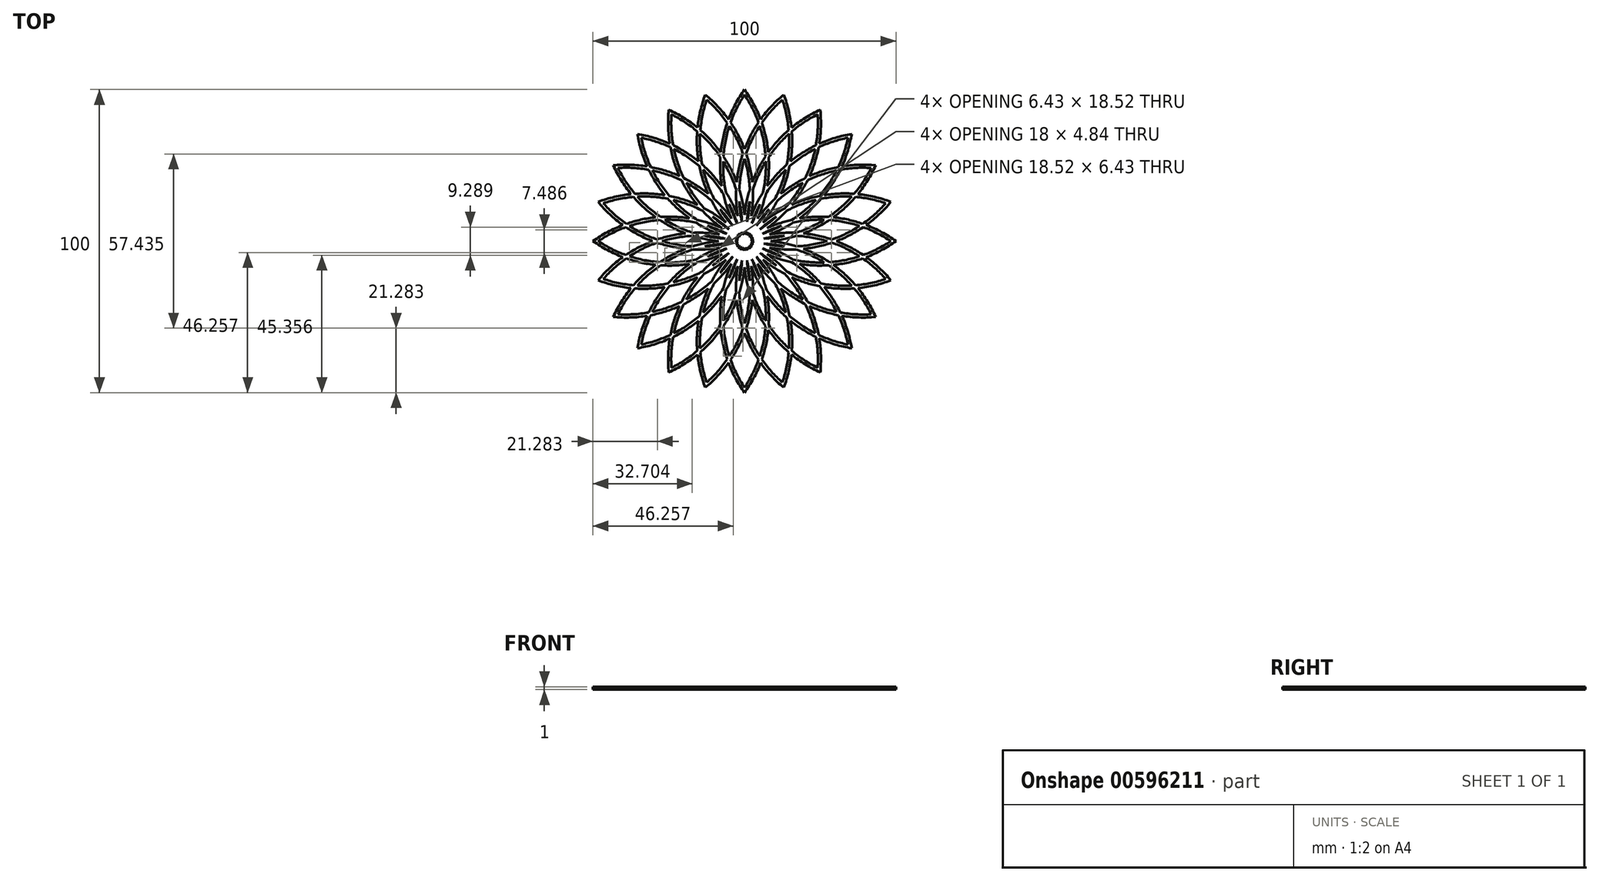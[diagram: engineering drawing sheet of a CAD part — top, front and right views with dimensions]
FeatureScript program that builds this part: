
annotation { "Feature Type Name" : "Feature", "Feature Type Description" : "" }
export const myFeature = defineFeature(function(context is Context, id is Id, definition is map)
    precondition{}
    {
        {
            var Q0;
            Q0=qCreatedBy(makeId("Top.planeOp"),FACE);
            var sketch = newSketch(context, id + "F0", { "sketchPlane" : qUnion([Q0])});
            skArc(sketch, "E0.1", {"start": v(0.29, 2.19) * mm, "mid": v(0.55, 2.6) * mm, "end": v(0.8, 3) * mm});
            skArc(sketch, "E1.22.1", {"start": v(24.12, 41.78) * mm, "mid": v(19.7, 39.26) * mm, "end": v(15.6, 36.21) * mm});
            skArc(sketch, "E1.22.3", {"start": v(25, 43.3) * mm, "mid": v(20.06, 40.68) * mm, "end": v(15.5, 37.43) * mm});
            skArc(sketch, "E1.23.1", {"start": v(12.49, 46.6) * mm, "mid": v(8.86, 43.02) * mm, "end": v(5.7, 39.02) * mm});
            skArc(sketch, "E1.23.3", {"start": v(12.94, 48.3) * mm, "mid": v(8.85, 44.48) * mm, "end": v(5.29, 40.16) * mm});
            skPoint(sketch, "E1.center", {"position": v(0, 0) * mm});
            skLineSegment(sketch, "E2", {"start": v(25, 43.3) * mm, "end": v(0, 0) * mm, "construction": true});
            skArc(sketch, "E3.trimOffspring", {"start": v(4.6, 39.17) * mm, "mid": v(2.04, 34.88) * mm, "end": v(0, 30.33) * mm});
            skArc(sketch, "E4.trimOffspring", {"start": v(5.29, 40.16) * mm, "mid": v(2.97, 45.26) * mm, "end": v(0, 50) * mm});
            skArc(sketch, "E5.trimOffspring", {"start": v(4.6, 39.17) * mm, "mid": v(2.57, 43.85) * mm, "end": v(0, 48.25) * mm});
            skArc(sketch, "E6.trimOffspring", {"start": v(5, 37.98) * mm, "mid": v(2.49, 33.55) * mm, "end": v(0.53, 28.85) * mm});
            skArc(sketch, "E7.trimOffspring", {"start": v(14.57, 36.64) * mm, "mid": v(11, 33.17) * mm, "end": v(7.85, 29.3) * mm});
            skArc(sketch, "E8.trimOffspring", {"start": v(15.5, 37.43) * mm, "mid": v(14.58, 42.95) * mm, "end": v(12.94, 48.3) * mm});
            skArc(sketch, "E9.trimOffspring", {"start": v(14.66, 35.39) * mm, "mid": v(11.08, 31.76) * mm, "end": v(7.98, 27.73) * mm});
            skArc(sketch, "E10.trimOffspring", {"start": v(14.57, 36.64) * mm, "mid": v(13.83, 41.69) * mm, "end": v(12.49, 46.6) * mm});
            skArc(sketch, "E11.trimOffspring", {"start": v(7.85, 29.3) * mm, "mid": v(7.06, 34.22) * mm, "end": v(5.7, 39.02) * mm});
            skArc(sketch, "E12.trimOffspring", {"start": v(6.96, 28) * mm, "mid": v(4.52, 23.86) * mm, "end": v(2.56, 19.46) * mm});
            skArc(sketch, "E13.trimOffspring", {"start": v(6.96, 28) * mm, "mid": v(6.28, 33.05) * mm, "end": v(5, 37.98) * mm});
            skArc(sketch, "E14.trimOffspring", {"start": v(7.05, 26.3) * mm, "mid": v(4.6, 21.75) * mm, "end": v(2.74, 16.93) * mm});
            skArc(sketch, "E15.trimOffspring", {"start": v(13.97, 25.25) * mm, "mid": v(10.54, 21.87) * mm, "end": v(7.51, 18.13) * mm});
            skArc(sketch, "E16.trimOffspring", {"start": v(13.97, 25.25) * mm, "mid": v(14.62, 30.3) * mm, "end": v(14.66, 35.39) * mm});
            skArc(sketch, "E17.trimOffspring", {"start": v(2.56, 19.46) * mm, "mid": v(1.8, 24.21) * mm, "end": v(0.53, 28.85) * mm});
            skArc(sketch, "E18.trimOffspring", {"start": v(1.73, 17.07) * mm, "mid": v(0.65, 12.87) * mm, "end": v(0, 8.59) * mm});
            skArc(sketch, "E19.trimOffspring", {"start": v(1.73, 17.07) * mm, "mid": v(1.18, 22.2) * mm, "end": v(0, 27.22) * mm});
            skArc(sketch, "E20.trimOffspring", {"start": v(1.73, 13.13) * mm, "mid": v(1.14, 9.75) * mm, "end": v(0.83, 6.33) * mm});
            skArc(sketch, "E21.trimOffspring", {"start": v(6.1, 16.04) * mm, "mid": v(3.96, 12.26) * mm, "end": v(2.22, 8.3) * mm});
            skArc(sketch, "E22.trimOffspring", {"start": v(7.51, 18.13) * mm, "mid": v(8.02, 22.92) * mm, "end": v(7.98, 27.73) * mm});
            skArc(sketch, "E23.trimOffspring", {"start": v(6.1, 16.04) * mm, "mid": v(6.89, 21.14) * mm, "end": v(7.05, 26.3) * mm});
            skArc(sketch, "E24.trimOffspring", {"start": v(5.07, 12.23) * mm, "mid": v(3.63, 9.12) * mm, "end": v(2.44, 5.9) * mm});
            skArc(sketch, "E25.trimOffspring", {"start": v(2.44, 5.9) * mm, "mid": v(3.89, 9.01) * mm, "end": v(5.07, 12.23) * mm});
            skArc(sketch, "E26.trimOffspring", {"start": v(2.22, 8.3) * mm, "mid": v(2.7, 12.6) * mm, "end": v(2.74, 16.93) * mm});
            skArc(sketch, "E27.trimOffspring", {"start": v(0.83, 6.33) * mm, "mid": v(1.42, 9.71) * mm, "end": v(1.73, 13.13) * mm});
            skArc(sketch, "E28.trimOffspring", {"start": v(0.8, 3) * mm, "mid": v(0.82, 2.52) * mm, "end": v(0.84, 2.04) * mm});
            skArc(sketch, "E29.trimOffspring", {"start": v(0.84, 2.04) * mm, "mid": v(1.2, 2.36) * mm, "end": v(1.55, 2.69) * mm});
            skArc(sketch, "E30.trimOffspring", {"start": v(4.3, 7.44) * mm, "mid": v(5.87, 11.47) * mm, "end": v(7.03, 15.65) * mm});
            skLineSegment(sketch, "E31", {"start": v(0, 0) * mm, "end": v(0, 50) * mm, "construction": true});
            skLineSegment(sketch, "E32", {"start": v(0.29, 2.19) * mm, "end": v(0, 3.1) * mm});
            skArc(sketch, "E33.trimOffspring", {"start": v(13.61, 23.58) * mm, "mid": v(10.08, 19.81) * mm, "end": v(7.03, 15.65) * mm});
            skArc(sketch, "E34.trimOffspring", {"start": v(15.16, 26.27) * mm, "mid": v(15.68, 31.23) * mm, "end": v(15.6, 36.21) * mm});
            skPoint(sketch, "E35.orphan", {"position": v(1.24, 1.24) * mm});
            skArc(sketch, "E36.1.0", {"start": v(-7.51, 18.13) * mm, "mid": v(-10.54, 21.87) * mm, "end": v(-13.97, 25.25) * mm});
            skArc(sketch, "E36.1.1", {"start": v(-0.53, 28.85) * mm, "mid": v(-1.8, 24.21) * mm, "end": v(-2.56, 19.46) * mm});
            skArc(sketch, "E36.1.2", {"start": v(-12.94, 48.3) * mm, "mid": v(-14.58, 42.95) * mm, "end": v(-15.5, 37.43) * mm});
            skArc(sketch, "E36.1.3", {"start": v(-7.85, 29.3) * mm, "mid": v(-11, 33.17) * mm, "end": v(-14.57, 36.64) * mm});
            skArc(sketch, "E36.1.4", {"start": v(-12.49, 46.6) * mm, "mid": v(-13.83, 41.69) * mm, "end": v(-14.57, 36.64) * mm});
            skArc(sketch, "E36.1.5", {"start": v(-14.66, 35.39) * mm, "mid": v(-14.62, 30.3) * mm, "end": v(-13.97, 25.25) * mm});
            skArc(sketch, "E36.1.6", {"start": v(-2.56, 19.46) * mm, "mid": v(-4.52, 23.86) * mm, "end": v(-6.96, 28) * mm});
            skArc(sketch, "E36.1.7", {"start": v(-5, 37.98) * mm, "mid": v(-6.28, 33.05) * mm, "end": v(-6.96, 28) * mm});
            skArc(sketch, "E36.1.8", {"start": v(-0.83, 6.33) * mm, "mid": v(-1.14, 9.75) * mm, "end": v(-1.73, 13.13) * mm});
            skArc(sketch, "E36.1.9", {"start": v(-5.7, 39.02) * mm, "mid": v(-8.86, 43.02) * mm, "end": v(-12.49, 46.6) * mm});
            skArc(sketch, "E36.1.10", {"start": v(-2.74, 16.93) * mm, "mid": v(-4.6, 21.75) * mm, "end": v(-7.05, 26.3) * mm});
            skArc(sketch, "E36.1.11", {"start": v(-0.53, 28.85) * mm, "mid": v(-2.49, 33.55) * mm, "end": v(-5, 37.98) * mm});
            skLineSegment(sketch, "E36.1.12", {"start": v(0, 0) * mm, "end": v(-25, 43.3) * mm, "construction": true});
            skArc(sketch, "E36.1.13", {"start": v(0, 8.59) * mm, "mid": v(-0.65, 12.87) * mm, "end": v(-1.73, 17.07) * mm});
            skArc(sketch, "E36.1.15", {"start": v(-2.22, 8.3) * mm, "mid": v(-3.96, 12.26) * mm, "end": v(-6.1, 16.04) * mm});
            skArc(sketch, "E36.1.16", {"start": v(-7.03, 15.65) * mm, "mid": v(-10.08, 19.81) * mm, "end": v(-13.61, 23.58) * mm});
            skArc(sketch, "E36.1.17", {"start": v(0, 50) * mm, "mid": v(-2.97, 45.26) * mm, "end": v(-5.29, 40.16) * mm});
            skArc(sketch, "E36.1.18", {"start": v(-7.05, 26.3) * mm, "mid": v(-6.89, 21.14) * mm, "end": v(-6.1, 16.04) * mm});
            skArc(sketch, "E36.1.19", {"start": v(0, 30.33) * mm, "mid": v(-2.04, 34.88) * mm, "end": v(-4.6, 39.17) * mm});
            skArc(sketch, "E36.1.20", {"start": v(-5.7, 39.02) * mm, "mid": v(-7.06, 34.22) * mm, "end": v(-7.85, 29.3) * mm});
            skArc(sketch, "E36.1.21", {"start": v(-15.6, 36.21) * mm, "mid": v(-19.7, 39.26) * mm, "end": v(-24.12, 41.78) * mm});
            skArc(sketch, "E36.1.22", {"start": v(-15.5, 37.43) * mm, "mid": v(-20.06, 40.68) * mm, "end": v(-25, 43.3) * mm});
            skLineSegment(sketch, "E36.1.23", {"start": v(0, 50) * mm, "end": v(0, 0) * mm, "construction": true});
            skArc(sketch, "E36.1.24", {"start": v(-2.44, 5.9) * mm, "mid": v(-3.63, 9.12) * mm, "end": v(-5.07, 12.23) * mm});
            skArc(sketch, "E36.1.25", {"start": v(-7.98, 27.73) * mm, "mid": v(-8.02, 22.92) * mm, "end": v(-7.51, 18.13) * mm});
            skArc(sketch, "E36.1.26", {"start": v(0, 27.22) * mm, "mid": v(-1.18, 22.2) * mm, "end": v(-1.73, 17.07) * mm});
            skArc(sketch, "E36.1.27", {"start": v(-7.03, 15.65) * mm, "mid": v(-5.87, 11.47) * mm, "end": v(-4.3, 7.44) * mm});
            skArc(sketch, "E36.1.28", {"start": v(-5.29, 40.16) * mm, "mid": v(-8.85, 44.48) * mm, "end": v(-12.94, 48.3) * mm});
            skArc(sketch, "E36.1.29", {"start": v(-1.73, 13.13) * mm, "mid": v(-1.42, 9.71) * mm, "end": v(-0.83, 6.33) * mm});
            skArc(sketch, "E36.1.30", {"start": v(-2.74, 16.93) * mm, "mid": v(-2.7, 12.6) * mm, "end": v(-2.22, 8.3) * mm});
            skArc(sketch, "E36.1.31", {"start": v(-7.98, 27.73) * mm, "mid": v(-11.08, 31.76) * mm, "end": v(-14.66, 35.39) * mm});
            skPoint(sketch, "E36.1.32", {"position": v(0.45, 1.7) * mm});
            skArc(sketch, "E36.1.33", {"start": v(-15.6, 36.21) * mm, "mid": v(-15.68, 31.23) * mm, "end": v(-15.16, 26.27) * mm});
            skArc(sketch, "E36.1.34", {"start": v(0, 48.25) * mm, "mid": v(-2.57, 43.85) * mm, "end": v(-4.6, 39.17) * mm});
            skArc(sketch, "E36.1.35", {"start": v(-5.07, 12.23) * mm, "mid": v(-3.89, 9.01) * mm, "end": v(-2.44, 5.9) * mm});
            skArc(sketch, "E36.1.36", {"start": v(-0.8, 3) * mm, "mid": v(-0.55, 2.6) * mm, "end": v(-0.29, 2.19) * mm});
            skLineSegment(sketch, "E36.1.37", {"start": v(-0.84, 2.04) * mm, "end": v(-1.55, 2.69) * mm});
            skArc(sketch, "E36.1.38", {"start": v(-0.29, 2.19) * mm, "mid": v(-0.14, 2.65) * mm, "end": v(0, 3.1) * mm});
            skArc(sketch, "E36.1.39", {"start": v(-0.84, 2.04) * mm, "mid": v(-0.82, 2.52) * mm, "end": v(-0.8, 3) * mm});
            skArc(sketch, "E36.2.0", {"start": v(-15.57, 11.95) * mm, "mid": v(-20.06, 13.67) * mm, "end": v(-24.72, 14.88) * mm});
            skArc(sketch, "E36.2.1", {"start": v(-14.88, 24.72) * mm, "mid": v(-13.67, 20.06) * mm, "end": v(-11.95, 15.57) * mm});
            skArc(sketch, "E36.2.2", {"start": v(-35.36, 35.36) * mm, "mid": v(-34.1, 29.9) * mm, "end": v(-32.14, 24.66) * mm});
            skArc(sketch, "E36.2.3", {"start": v(-21.45, 21.45) * mm, "mid": v(-26.1, 23.22) * mm, "end": v(-30.94, 24.45) * mm});
            skArc(sketch, "E36.2.4", {"start": v(-34.12, 34.12) * mm, "mid": v(-32.82, 29.19) * mm, "end": v(-30.94, 24.45) * mm});
            skArc(sketch, "E36.2.5", {"start": v(-30.39, 23.32) * mm, "mid": v(-27.81, 18.93) * mm, "end": v(-24.72, 14.88) * mm});
            skArc(sketch, "E36.2.6", {"start": v(-11.95, 15.57) * mm, "mid": v(-15.84, 18.4) * mm, "end": v(-20.03, 20.78) * mm});
            skArc(sketch, "E36.2.7", {"start": v(-23.32, 30.39) * mm, "mid": v(-21.97, 25.48) * mm, "end": v(-20.03, 20.78) * mm});
            skArc(sketch, "E36.2.8", {"start": v(-3.89, 5.07) * mm, "mid": v(-5.86, 7.87) * mm, "end": v(-8.06, 10.5) * mm});
            skArc(sketch, "E36.2.9", {"start": v(-24.45, 30.94) * mm, "mid": v(-29.19, 32.82) * mm, "end": v(-34.12, 34.12) * mm});
            skArc(sketch, "E36.2.10", {"start": v(-10.84, 13.3) * mm, "mid": v(-14.86, 16.53) * mm, "end": v(-19.25, 19.25) * mm});
            skArc(sketch, "E36.2.11", {"start": v(-14.88, 24.72) * mm, "mid": v(-18.93, 27.81) * mm, "end": v(-23.32, 30.39) * mm});
            skLineSegment(sketch, "E36.2.12", {"start": v(0, 0) * mm, "end": v(-43.3, 25) * mm, "construction": true});
            skArc(sketch, "E36.2.13", {"start": v(-4.3, 7.44) * mm, "mid": v(-7, 10.82) * mm, "end": v(-10.04, 13.91) * mm});
            skArc(sketch, "E36.2.15", {"start": v(-6.07, 6.07) * mm, "mid": v(-9.56, 8.64) * mm, "end": v(-13.3, 10.84) * mm});
            skArc(sketch, "E36.2.16", {"start": v(-13.91, 10.04) * mm, "mid": v(-18.63, 12.12) * mm, "end": v(-23.58, 13.61) * mm});
            skArc(sketch, "E36.2.17", {"start": v(-25, 43.3) * mm, "mid": v(-25.2, 37.7) * mm, "end": v(-24.66, 32.14) * mm});
            skArc(sketch, "E36.2.18", {"start": v(-19.25, 19.25) * mm, "mid": v(-16.53, 14.86) * mm, "end": v(-13.3, 10.84) * mm});
            skArc(sketch, "E36.2.19", {"start": v(-15.16, 26.27) * mm, "mid": v(-19.2, 29.19) * mm, "end": v(-23.56, 31.62) * mm});
            skArc(sketch, "E36.2.20", {"start": v(-24.45, 30.94) * mm, "mid": v(-23.22, 26.1) * mm, "end": v(-21.45, 21.45) * mm});
            skArc(sketch, "E36.2.21", {"start": v(-31.62, 23.56) * mm, "mid": v(-36.69, 24.15) * mm, "end": v(-41.78, 24.12) * mm});
            skArc(sketch, "E36.2.22", {"start": v(-32.14, 24.66) * mm, "mid": v(-37.7, 25.2) * mm, "end": v(-43.3, 25) * mm});
            skLineSegment(sketch, "E36.2.23", {"start": v(-25, 43.3) * mm, "end": v(0, 0) * mm, "construction": true});
            skArc(sketch, "E36.2.24", {"start": v(-5.07, 3.89) * mm, "mid": v(-7.7, 6.09) * mm, "end": v(-10.5, 8.06) * mm});
            skArc(sketch, "E36.2.25", {"start": v(-20.78, 20.03) * mm, "mid": v(-18.4, 15.84) * mm, "end": v(-15.57, 11.95) * mm});
            skArc(sketch, "E36.2.26", {"start": v(-13.61, 23.58) * mm, "mid": v(-12.12, 18.63) * mm, "end": v(-10.04, 13.91) * mm});
            skArc(sketch, "E36.2.27", {"start": v(-13.91, 10.04) * mm, "mid": v(-10.82, 7) * mm, "end": v(-7.44, 4.3) * mm});
            skArc(sketch, "E36.2.28", {"start": v(-24.66, 32.14) * mm, "mid": v(-29.9, 34.1) * mm, "end": v(-35.36, 35.36) * mm});
            skArc(sketch, "E36.2.29", {"start": v(-8.06, 10.5) * mm, "mid": v(-6.09, 7.7) * mm, "end": v(-3.89, 5.07) * mm});
            skArc(sketch, "E36.2.30", {"start": v(-10.84, 13.3) * mm, "mid": v(-8.64, 9.56) * mm, "end": v(-6.07, 6.07) * mm});
            skArc(sketch, "E36.2.31", {"start": v(-20.78, 20.03) * mm, "mid": v(-25.48, 21.97) * mm, "end": v(-30.39, 23.32) * mm});
            skPoint(sketch, "E36.2.32", {"position": v(-0.45, 1.7) * mm});
            skArc(sketch, "E36.2.33", {"start": v(-31.62, 23.56) * mm, "mid": v(-29.19, 19.2) * mm, "end": v(-26.27, 15.16) * mm});
            skArc(sketch, "E36.2.34", {"start": v(-24.12, 41.78) * mm, "mid": v(-24.15, 36.69) * mm, "end": v(-23.56, 31.62) * mm});
            skArc(sketch, "E36.2.35", {"start": v(-10.5, 8.06) * mm, "mid": v(-7.87, 5.86) * mm, "end": v(-5.07, 3.89) * mm});
            skArc(sketch, "E36.2.36", {"start": v(-2.2, 2.2) * mm, "mid": v(-1.77, 1.97) * mm, "end": v(-1.34, 1.75) * mm});
            skLineSegment(sketch, "E36.2.37", {"start": v(-1.75, 1.34) * mm, "end": v(-2.69, 1.55) * mm});
            skArc(sketch, "E36.2.38", {"start": v(-1.34, 1.75) * mm, "mid": v(-1.45, 2.22) * mm, "end": v(-1.55, 2.69) * mm});
            skArc(sketch, "E36.2.39", {"start": v(-1.75, 1.34) * mm, "mid": v(-1.97, 1.77) * mm, "end": v(-2.2, 2.2) * mm});
            skArc(sketch, "E36.3.0", {"start": v(-19.46, 2.56) * mm, "mid": v(-24.21, 1.8) * mm, "end": v(-28.85, 0.53) * mm});
            skArc(sketch, "E36.3.1", {"start": v(-25.25, 13.97) * mm, "mid": v(-21.87, 10.54) * mm, "end": v(-18.13, 7.51) * mm});
            skArc(sketch, "E36.3.2", {"start": v(-48.3, 12.94) * mm, "mid": v(-44.48, 8.85) * mm, "end": v(-40.16, 5.29) * mm});
            skArc(sketch, "E36.3.3", {"start": v(-29.3, 7.85) * mm, "mid": v(-34.22, 7.06) * mm, "end": v(-39.02, 5.7) * mm});
            skArc(sketch, "E36.3.4", {"start": v(-46.6, 12.49) * mm, "mid": v(-43.02, 8.86) * mm, "end": v(-39.02, 5.7) * mm});
            skArc(sketch, "E36.3.5", {"start": v(-37.98, 5) * mm, "mid": v(-33.55, 2.49) * mm, "end": v(-28.85, 0.53) * mm});
            skArc(sketch, "E36.3.6", {"start": v(-18.13, 7.51) * mm, "mid": v(-22.92, 8.02) * mm, "end": v(-27.73, 7.98) * mm});
            skArc(sketch, "E36.3.7", {"start": v(-35.39, 14.66) * mm, "mid": v(-31.76, 11.08) * mm, "end": v(-27.73, 7.98) * mm});
            skArc(sketch, "E36.3.8", {"start": v(-5.9, 2.44) * mm, "mid": v(-9.01, 3.89) * mm, "end": v(-12.23, 5.07) * mm});
            skArc(sketch, "E36.3.9", {"start": v(-36.64, 14.57) * mm, "mid": v(-41.69, 13.83) * mm, "end": v(-46.6, 12.49) * mm});
            skArc(sketch, "E36.3.10", {"start": v(-16.04, 6.1) * mm, "mid": v(-21.14, 6.89) * mm, "end": v(-26.3, 7.05) * mm});
            skArc(sketch, "E36.3.11", {"start": v(-25.25, 13.97) * mm, "mid": v(-30.3, 14.62) * mm, "end": v(-35.39, 14.66) * mm});
            skLineSegment(sketch, "E36.3.12", {"start": v(0, 0) * mm, "end": v(-50, 0) * mm, "construction": true});
            skArc(sketch, "E36.3.13", {"start": v(-7.44, 4.3) * mm, "mid": v(-11.47, 5.87) * mm, "end": v(-15.65, 7.03) * mm});
            skArc(sketch, "E36.3.15", {"start": v(-8.3, 2.22) * mm, "mid": v(-12.6, 2.7) * mm, "end": v(-16.93, 2.74) * mm});
            skArc(sketch, "E36.3.16", {"start": v(-17.07, 1.73) * mm, "mid": v(-22.2, 1.18) * mm, "end": v(-27.22, 0) * mm});
            skArc(sketch, "E36.3.17", {"start": v(-43.3, 25) * mm, "mid": v(-40.68, 20.06) * mm, "end": v(-37.43, 15.5) * mm});
            skArc(sketch, "E36.3.18", {"start": v(-26.3, 7.05) * mm, "mid": v(-21.75, 4.6) * mm, "end": v(-16.93, 2.74) * mm});
            skArc(sketch, "E36.3.19", {"start": v(-26.27, 15.16) * mm, "mid": v(-31.23, 15.68) * mm, "end": v(-36.21, 15.6) * mm});
            skArc(sketch, "E36.3.20", {"start": v(-36.64, 14.57) * mm, "mid": v(-33.17, 11) * mm, "end": v(-29.3, 7.85) * mm});
            skArc(sketch, "E36.3.21", {"start": v(-39.17, 4.6) * mm, "mid": v(-43.85, 2.57) * mm, "end": v(-48.25, 0) * mm});
            skArc(sketch, "E36.3.22", {"start": v(-40.16, 5.29) * mm, "mid": v(-45.26, 2.97) * mm, "end": v(-50, 0) * mm});
            skLineSegment(sketch, "E36.3.23", {"start": v(-43.3, 25) * mm, "end": v(0, 0) * mm, "construction": true});
            skArc(sketch, "E36.3.24", {"start": v(-6.33, 0.83) * mm, "mid": v(-9.71, 1.42) * mm, "end": v(-13.13, 1.73) * mm});
            skArc(sketch, "E36.3.25", {"start": v(-28, 6.96) * mm, "mid": v(-23.86, 4.52) * mm, "end": v(-19.46, 2.56) * mm});
            skArc(sketch, "E36.3.26", {"start": v(-23.58, 13.61) * mm, "mid": v(-19.81, 10.08) * mm, "end": v(-15.65, 7.03) * mm});
            skArc(sketch, "E36.3.27", {"start": v(-17.07, 1.73) * mm, "mid": v(-12.87, 0.65) * mm, "end": v(-8.59, 0) * mm});
            skArc(sketch, "E36.3.28", {"start": v(-37.43, 15.5) * mm, "mid": v(-42.95, 14.58) * mm, "end": v(-48.3, 12.94) * mm});
            skArc(sketch, "E36.3.29", {"start": v(-12.23, 5.07) * mm, "mid": v(-9.12, 3.63) * mm, "end": v(-5.9, 2.44) * mm});
            skArc(sketch, "E36.3.30", {"start": v(-16.04, 6.1) * mm, "mid": v(-12.26, 3.96) * mm, "end": v(-8.3, 2.22) * mm});
            skArc(sketch, "E36.3.31", {"start": v(-28, 6.96) * mm, "mid": v(-33.05, 6.28) * mm, "end": v(-37.98, 5) * mm});
            skPoint(sketch, "E36.3.32", {"position": v(-1.24, 1.24) * mm});
            skArc(sketch, "E36.3.33", {"start": v(-39.17, 4.6) * mm, "mid": v(-34.88, 2.04) * mm, "end": v(-30.33, 0) * mm});
            skArc(sketch, "E36.3.34", {"start": v(-41.78, 24.12) * mm, "mid": v(-39.26, 19.7) * mm, "end": v(-36.21, 15.6) * mm});
            skArc(sketch, "E36.3.35", {"start": v(-13.13, 1.73) * mm, "mid": v(-9.75, 1.14) * mm, "end": v(-6.33, 0.83) * mm});
            skArc(sketch, "E36.3.36", {"start": v(-3, 0.8) * mm, "mid": v(-2.52, 0.82) * mm, "end": v(-2.04, 0.84) * mm});
            skLineSegment(sketch, "E36.3.37", {"start": v(-2.19, 0.29) * mm, "end": v(-3.1, 0) * mm});
            skArc(sketch, "E36.3.38", {"start": v(-2.04, 0.84) * mm, "mid": v(-2.36, 1.2) * mm, "end": v(-2.69, 1.55) * mm});
            skArc(sketch, "E36.3.39", {"start": v(-2.19, 0.29) * mm, "mid": v(-2.6, 0.55) * mm, "end": v(-3, 0.8) * mm});
            skArc(sketch, "E36.4.0", {"start": v(-18.13, -7.51) * mm, "mid": v(-21.87, -10.54) * mm, "end": v(-25.25, -13.97) * mm});
            skArc(sketch, "E36.4.1", {"start": v(-28.85, -0.53) * mm, "mid": v(-24.21, -1.8) * mm, "end": v(-19.46, -2.56) * mm});
            skArc(sketch, "E36.4.2", {"start": v(-48.3, -12.94) * mm, "mid": v(-42.95, -14.58) * mm, "end": v(-37.43, -15.5) * mm});
            skArc(sketch, "E36.4.3", {"start": v(-29.3, -7.85) * mm, "mid": v(-33.17, -11) * mm, "end": v(-36.64, -14.57) * mm});
            skArc(sketch, "E36.4.4", {"start": v(-46.6, -12.49) * mm, "mid": v(-41.69, -13.83) * mm, "end": v(-36.64, -14.57) * mm});
            skArc(sketch, "E36.4.5", {"start": v(-35.39, -14.66) * mm, "mid": v(-30.3, -14.62) * mm, "end": v(-25.25, -13.97) * mm});
            skArc(sketch, "E36.4.6", {"start": v(-19.46, -2.56) * mm, "mid": v(-23.86, -4.52) * mm, "end": v(-28, -6.96) * mm});
            skArc(sketch, "E36.4.7", {"start": v(-37.98, -5) * mm, "mid": v(-33.05, -6.28) * mm, "end": v(-28, -6.96) * mm});
            skArc(sketch, "E36.4.8", {"start": v(-6.33, -0.83) * mm, "mid": v(-9.75, -1.14) * mm, "end": v(-13.13, -1.73) * mm});
            skArc(sketch, "E36.4.9", {"start": v(-39.02, -5.7) * mm, "mid": v(-43.02, -8.86) * mm, "end": v(-46.6, -12.49) * mm});
            skArc(sketch, "E36.4.10", {"start": v(-16.93, -2.74) * mm, "mid": v(-21.75, -4.6) * mm, "end": v(-26.3, -7.05) * mm});
            skArc(sketch, "E36.4.11", {"start": v(-28.85, -0.53) * mm, "mid": v(-33.55, -2.49) * mm, "end": v(-37.98, -5) * mm});
            skLineSegment(sketch, "E36.4.12", {"start": v(0, 0) * mm, "end": v(-43.3, -25) * mm, "construction": true});
            skArc(sketch, "E36.4.13", {"start": v(-8.59, 0) * mm, "mid": v(-12.87, -0.65) * mm, "end": v(-17.07, -1.73) * mm});
            skArc(sketch, "E36.4.15", {"start": v(-8.3, -2.22) * mm, "mid": v(-12.26, -3.96) * mm, "end": v(-16.04, -6.1) * mm});
            skArc(sketch, "E36.4.16", {"start": v(-15.65, -7.03) * mm, "mid": v(-19.81, -10.08) * mm, "end": v(-23.58, -13.61) * mm});
            skArc(sketch, "E36.4.17", {"start": v(-50, 0) * mm, "mid": v(-45.26, -2.97) * mm, "end": v(-40.16, -5.29) * mm});
            skArc(sketch, "E36.4.18", {"start": v(-26.3, -7.05) * mm, "mid": v(-21.14, -6.89) * mm, "end": v(-16.04, -6.1) * mm});
            skArc(sketch, "E36.4.19", {"start": v(-30.33, 0) * mm, "mid": v(-34.88, -2.04) * mm, "end": v(-39.17, -4.6) * mm});
            skArc(sketch, "E36.4.20", {"start": v(-39.02, -5.7) * mm, "mid": v(-34.22, -7.06) * mm, "end": v(-29.3, -7.85) * mm});
            skArc(sketch, "E36.4.21", {"start": v(-36.21, -15.6) * mm, "mid": v(-39.26, -19.7) * mm, "end": v(-41.78, -24.12) * mm});
            skArc(sketch, "E36.4.22", {"start": v(-37.43, -15.5) * mm, "mid": v(-40.68, -20.06) * mm, "end": v(-43.3, -25) * mm});
            skLineSegment(sketch, "E36.4.23", {"start": v(-50, 0) * mm, "end": v(0, 0) * mm, "construction": true});
            skArc(sketch, "E36.4.24", {"start": v(-5.9, -2.44) * mm, "mid": v(-9.12, -3.63) * mm, "end": v(-12.23, -5.07) * mm});
            skArc(sketch, "E36.4.25", {"start": v(-27.73, -7.98) * mm, "mid": v(-22.92, -8.02) * mm, "end": v(-18.13, -7.51) * mm});
            skArc(sketch, "E36.4.26", {"start": v(-27.22, 0) * mm, "mid": v(-22.2, -1.18) * mm, "end": v(-17.07, -1.73) * mm});
            skArc(sketch, "E36.4.27", {"start": v(-15.65, -7.03) * mm, "mid": v(-11.47, -5.87) * mm, "end": v(-7.44, -4.3) * mm});
            skArc(sketch, "E36.4.28", {"start": v(-40.16, -5.29) * mm, "mid": v(-44.48, -8.85) * mm, "end": v(-48.3, -12.94) * mm});
            skArc(sketch, "E36.4.29", {"start": v(-13.13, -1.73) * mm, "mid": v(-9.71, -1.42) * mm, "end": v(-6.33, -0.83) * mm});
            skArc(sketch, "E36.4.30", {"start": v(-16.93, -2.74) * mm, "mid": v(-12.6, -2.7) * mm, "end": v(-8.3, -2.22) * mm});
            skArc(sketch, "E36.4.31", {"start": v(-27.73, -7.98) * mm, "mid": v(-31.76, -11.08) * mm, "end": v(-35.39, -14.66) * mm});
            skPoint(sketch, "E36.4.32", {"position": v(-1.7, 0.45) * mm});
            skArc(sketch, "E36.4.33", {"start": v(-36.21, -15.6) * mm, "mid": v(-31.23, -15.68) * mm, "end": v(-26.27, -15.16) * mm});
            skArc(sketch, "E36.4.34", {"start": v(-48.25, 0) * mm, "mid": v(-43.85, -2.57) * mm, "end": v(-39.17, -4.6) * mm});
            skArc(sketch, "E36.4.35", {"start": v(-12.23, -5.07) * mm, "mid": v(-9.01, -3.89) * mm, "end": v(-5.9, -2.44) * mm});
            skArc(sketch, "E36.4.36", {"start": v(-3, -0.8) * mm, "mid": v(-2.6, -0.55) * mm, "end": v(-2.19, -0.29) * mm});
            skLineSegment(sketch, "E36.4.37", {"start": v(-2.04, -0.84) * mm, "end": v(-2.69, -1.55) * mm});
            skArc(sketch, "E36.4.38", {"start": v(-2.19, -0.29) * mm, "mid": v(-2.65, -0.14) * mm, "end": v(-3.1, 0) * mm});
            skArc(sketch, "E36.4.39", {"start": v(-2.04, -0.84) * mm, "mid": v(-2.52, -0.82) * mm, "end": v(-3, -0.8) * mm});
            skArc(sketch, "E36.5.0", {"start": v(-11.95, -15.57) * mm, "mid": v(-13.67, -20.06) * mm, "end": v(-14.88, -24.72) * mm});
            skArc(sketch, "E36.5.1", {"start": v(-24.72, -14.88) * mm, "mid": v(-20.06, -13.67) * mm, "end": v(-15.57, -11.95) * mm});
            skArc(sketch, "E36.5.2", {"start": v(-35.36, -35.36) * mm, "mid": v(-29.9, -34.1) * mm, "end": v(-24.66, -32.14) * mm});
            skArc(sketch, "E36.5.3", {"start": v(-21.45, -21.45) * mm, "mid": v(-23.22, -26.1) * mm, "end": v(-24.45, -30.94) * mm});
            skArc(sketch, "E36.5.4", {"start": v(-34.12, -34.12) * mm, "mid": v(-29.19, -32.82) * mm, "end": v(-24.45, -30.94) * mm});
            skArc(sketch, "E36.5.5", {"start": v(-23.32, -30.39) * mm, "mid": v(-18.93, -27.81) * mm, "end": v(-14.88, -24.72) * mm});
            skArc(sketch, "E36.5.6", {"start": v(-15.57, -11.95) * mm, "mid": v(-18.4, -15.84) * mm, "end": v(-20.78, -20.03) * mm});
            skArc(sketch, "E36.5.7", {"start": v(-30.39, -23.32) * mm, "mid": v(-25.48, -21.97) * mm, "end": v(-20.78, -20.03) * mm});
            skArc(sketch, "E36.5.8", {"start": v(-5.07, -3.89) * mm, "mid": v(-7.87, -5.86) * mm, "end": v(-10.5, -8.06) * mm});
            skArc(sketch, "E36.5.9", {"start": v(-30.94, -24.45) * mm, "mid": v(-32.82, -29.19) * mm, "end": v(-34.12, -34.12) * mm});
            skArc(sketch, "E36.5.10", {"start": v(-13.3, -10.84) * mm, "mid": v(-16.53, -14.86) * mm, "end": v(-19.25, -19.25) * mm});
            skArc(sketch, "E36.5.11", {"start": v(-24.72, -14.88) * mm, "mid": v(-27.81, -18.93) * mm, "end": v(-30.39, -23.32) * mm});
            skLineSegment(sketch, "E36.5.12", {"start": v(0, 0) * mm, "end": v(-25, -43.3) * mm, "construction": true});
            skArc(sketch, "E36.5.13", {"start": v(-7.44, -4.3) * mm, "mid": v(-10.82, -7) * mm, "end": v(-13.91, -10.04) * mm});
            skArc(sketch, "E36.5.15", {"start": v(-6.07, -6.07) * mm, "mid": v(-8.64, -9.56) * mm, "end": v(-10.84, -13.3) * mm});
            skArc(sketch, "E36.5.16", {"start": v(-10.04, -13.91) * mm, "mid": v(-12.12, -18.63) * mm, "end": v(-13.61, -23.58) * mm});
            skArc(sketch, "E36.5.17", {"start": v(-43.3, -25) * mm, "mid": v(-37.7, -25.2) * mm, "end": v(-32.14, -24.66) * mm});
            skArc(sketch, "E36.5.18", {"start": v(-19.25, -19.25) * mm, "mid": v(-14.86, -16.53) * mm, "end": v(-10.84, -13.3) * mm});
            skArc(sketch, "E36.5.19", {"start": v(-26.27, -15.16) * mm, "mid": v(-29.19, -19.2) * mm, "end": v(-31.62, -23.56) * mm});
            skArc(sketch, "E36.5.20", {"start": v(-30.94, -24.45) * mm, "mid": v(-26.1, -23.22) * mm, "end": v(-21.45, -21.45) * mm});
            skArc(sketch, "E36.5.21", {"start": v(-23.56, -31.62) * mm, "mid": v(-24.15, -36.69) * mm, "end": v(-24.12, -41.78) * mm});
            skArc(sketch, "E36.5.22", {"start": v(-24.66, -32.14) * mm, "mid": v(-25.2, -37.7) * mm, "end": v(-25, -43.3) * mm});
            skLineSegment(sketch, "E36.5.23", {"start": v(-43.3, -25) * mm, "end": v(0, 0) * mm, "construction": true});
            skArc(sketch, "E36.5.24", {"start": v(-3.89, -5.07) * mm, "mid": v(-6.09, -7.7) * mm, "end": v(-8.06, -10.5) * mm});
            skArc(sketch, "E36.5.25", {"start": v(-20.03, -20.78) * mm, "mid": v(-15.84, -18.4) * mm, "end": v(-11.95, -15.57) * mm});
            skArc(sketch, "E36.5.26", {"start": v(-23.58, -13.61) * mm, "mid": v(-18.63, -12.12) * mm, "end": v(-13.91, -10.04) * mm});
            skArc(sketch, "E36.5.27", {"start": v(-10.04, -13.91) * mm, "mid": v(-7, -10.82) * mm, "end": v(-4.3, -7.44) * mm});
            skArc(sketch, "E36.5.28", {"start": v(-32.14, -24.66) * mm, "mid": v(-34.1, -29.9) * mm, "end": v(-35.36, -35.36) * mm});
            skArc(sketch, "E36.5.29", {"start": v(-10.5, -8.06) * mm, "mid": v(-7.7, -6.09) * mm, "end": v(-5.07, -3.89) * mm});
            skArc(sketch, "E36.5.30", {"start": v(-13.3, -10.84) * mm, "mid": v(-9.56, -8.64) * mm, "end": v(-6.07, -6.07) * mm});
            skArc(sketch, "E36.5.31", {"start": v(-20.03, -20.78) * mm, "mid": v(-21.97, -25.48) * mm, "end": v(-23.32, -30.39) * mm});
            skPoint(sketch, "E36.5.32", {"position": v(-1.7, -0.45) * mm});
            skArc(sketch, "E36.5.33", {"start": v(-23.56, -31.62) * mm, "mid": v(-19.2, -29.19) * mm, "end": v(-15.16, -26.27) * mm});
            skArc(sketch, "E36.5.34", {"start": v(-41.78, -24.12) * mm, "mid": v(-36.69, -24.15) * mm, "end": v(-31.62, -23.56) * mm});
            skArc(sketch, "E36.5.35", {"start": v(-8.06, -10.5) * mm, "mid": v(-5.86, -7.87) * mm, "end": v(-3.89, -5.07) * mm});
            skArc(sketch, "E36.5.36", {"start": v(-2.2, -2.2) * mm, "mid": v(-1.97, -1.77) * mm, "end": v(-1.75, -1.34) * mm});
            skLineSegment(sketch, "E36.5.37", {"start": v(-1.34, -1.75) * mm, "end": v(-1.55, -2.69) * mm});
            skArc(sketch, "E36.5.38", {"start": v(-1.75, -1.34) * mm, "mid": v(-2.22, -1.45) * mm, "end": v(-2.69, -1.55) * mm});
            skArc(sketch, "E36.5.39", {"start": v(-1.34, -1.75) * mm, "mid": v(-1.77, -1.97) * mm, "end": v(-2.2, -2.2) * mm});
            skArc(sketch, "E36.6.0", {"start": v(-2.56, -19.46) * mm, "mid": v(-1.8, -24.21) * mm, "end": v(-0.53, -28.85) * mm});
            skArc(sketch, "E36.6.1", {"start": v(-13.97, -25.25) * mm, "mid": v(-10.54, -21.87) * mm, "end": v(-7.51, -18.13) * mm});
            skArc(sketch, "E36.6.2", {"start": v(-12.94, -48.3) * mm, "mid": v(-8.85, -44.48) * mm, "end": v(-5.29, -40.16) * mm});
            skArc(sketch, "E36.6.3", {"start": v(-7.85, -29.3) * mm, "mid": v(-7.06, -34.22) * mm, "end": v(-5.7, -39.02) * mm});
            skArc(sketch, "E36.6.4", {"start": v(-12.49, -46.6) * mm, "mid": v(-8.86, -43.02) * mm, "end": v(-5.7, -39.02) * mm});
            skArc(sketch, "E36.6.5", {"start": v(-5, -37.98) * mm, "mid": v(-2.49, -33.55) * mm, "end": v(-0.53, -28.85) * mm});
            skArc(sketch, "E36.6.6", {"start": v(-7.51, -18.13) * mm, "mid": v(-8.02, -22.92) * mm, "end": v(-7.98, -27.73) * mm});
            skArc(sketch, "E36.6.7", {"start": v(-14.66, -35.39) * mm, "mid": v(-11.08, -31.76) * mm, "end": v(-7.98, -27.73) * mm});
            skArc(sketch, "E36.6.8", {"start": v(-2.44, -5.9) * mm, "mid": v(-3.89, -9.01) * mm, "end": v(-5.07, -12.23) * mm});
            skArc(sketch, "E36.6.9", {"start": v(-14.57, -36.64) * mm, "mid": v(-13.83, -41.69) * mm, "end": v(-12.49, -46.6) * mm});
            skArc(sketch, "E36.6.10", {"start": v(-6.1, -16.04) * mm, "mid": v(-6.89, -21.14) * mm, "end": v(-7.05, -26.3) * mm});
            skArc(sketch, "E36.6.11", {"start": v(-13.97, -25.25) * mm, "mid": v(-14.62, -30.3) * mm, "end": v(-14.66, -35.39) * mm});
            skLineSegment(sketch, "E36.6.12", {"start": v(0, 0) * mm, "end": v(0, -50) * mm, "construction": true});
            skArc(sketch, "E36.6.13", {"start": v(-4.3, -7.44) * mm, "mid": v(-5.87, -11.47) * mm, "end": v(-7.03, -15.65) * mm});
            skArc(sketch, "E36.6.15", {"start": v(-2.22, -8.3) * mm, "mid": v(-2.7, -12.6) * mm, "end": v(-2.74, -16.93) * mm});
            skArc(sketch, "E36.6.16", {"start": v(-1.73, -17.07) * mm, "mid": v(-1.18, -22.2) * mm, "end": v(0, -27.22) * mm});
            skArc(sketch, "E36.6.17", {"start": v(-25, -43.3) * mm, "mid": v(-20.06, -40.68) * mm, "end": v(-15.5, -37.43) * mm});
            skArc(sketch, "E36.6.18", {"start": v(-7.05, -26.3) * mm, "mid": v(-4.6, -21.75) * mm, "end": v(-2.74, -16.93) * mm});
            skArc(sketch, "E36.6.19", {"start": v(-15.16, -26.27) * mm, "mid": v(-15.68, -31.23) * mm, "end": v(-15.6, -36.21) * mm});
            skArc(sketch, "E36.6.20", {"start": v(-14.57, -36.64) * mm, "mid": v(-11, -33.17) * mm, "end": v(-7.85, -29.3) * mm});
            skArc(sketch, "E36.6.21", {"start": v(-4.6, -39.17) * mm, "mid": v(-2.57, -43.85) * mm, "end": v(0, -48.25) * mm});
            skArc(sketch, "E36.6.22", {"start": v(-5.29, -40.16) * mm, "mid": v(-2.97, -45.26) * mm, "end": v(0, -50) * mm});
            skLineSegment(sketch, "E36.6.23", {"start": v(-25, -43.3) * mm, "end": v(0, 0) * mm, "construction": true});
            skArc(sketch, "E36.6.24", {"start": v(-0.83, -6.33) * mm, "mid": v(-1.42, -9.71) * mm, "end": v(-1.73, -13.13) * mm});
            skArc(sketch, "E36.6.25", {"start": v(-6.96, -28) * mm, "mid": v(-4.52, -23.86) * mm, "end": v(-2.56, -19.46) * mm});
            skArc(sketch, "E36.6.26", {"start": v(-13.61, -23.58) * mm, "mid": v(-10.08, -19.81) * mm, "end": v(-7.03, -15.65) * mm});
            skArc(sketch, "E36.6.27", {"start": v(-1.73, -17.07) * mm, "mid": v(-0.65, -12.87) * mm, "end": v(0, -8.59) * mm});
            skArc(sketch, "E36.6.28", {"start": v(-15.5, -37.43) * mm, "mid": v(-14.58, -42.95) * mm, "end": v(-12.94, -48.3) * mm});
            skArc(sketch, "E36.6.29", {"start": v(-5.07, -12.23) * mm, "mid": v(-3.63, -9.12) * mm, "end": v(-2.44, -5.9) * mm});
            skArc(sketch, "E36.6.30", {"start": v(-6.1, -16.04) * mm, "mid": v(-3.96, -12.26) * mm, "end": v(-2.22, -8.3) * mm});
            skArc(sketch, "E36.6.31", {"start": v(-6.96, -28) * mm, "mid": v(-6.28, -33.05) * mm, "end": v(-5, -37.98) * mm});
            skPoint(sketch, "E36.6.32", {"position": v(-1.24, -1.24) * mm});
            skArc(sketch, "E36.6.33", {"start": v(-4.6, -39.17) * mm, "mid": v(-2.04, -34.88) * mm, "end": v(0, -30.33) * mm});
            skArc(sketch, "E36.6.34", {"start": v(-24.12, -41.78) * mm, "mid": v(-19.7, -39.26) * mm, "end": v(-15.6, -36.21) * mm});
            skArc(sketch, "E36.6.35", {"start": v(-1.73, -13.13) * mm, "mid": v(-1.14, -9.75) * mm, "end": v(-0.83, -6.33) * mm});
            skArc(sketch, "E36.6.36", {"start": v(-0.8, -3) * mm, "mid": v(-0.82, -2.52) * mm, "end": v(-0.84, -2.04) * mm});
            skLineSegment(sketch, "E36.6.37", {"start": v(-0.29, -2.19) * mm, "end": v(0, -3.1) * mm});
            skArc(sketch, "E36.6.38", {"start": v(-0.84, -2.04) * mm, "mid": v(-1.2, -2.36) * mm, "end": v(-1.55, -2.69) * mm});
            skArc(sketch, "E36.6.39", {"start": v(-0.29, -2.19) * mm, "mid": v(-0.55, -2.6) * mm, "end": v(-0.8, -3) * mm});
            skArc(sketch, "E36.7.0", {"start": v(7.51, -18.13) * mm, "mid": v(10.54, -21.87) * mm, "end": v(13.97, -25.25) * mm});
            skArc(sketch, "E36.7.1", {"start": v(0.53, -28.85) * mm, "mid": v(1.8, -24.21) * mm, "end": v(2.56, -19.46) * mm});
            skArc(sketch, "E36.7.2", {"start": v(12.94, -48.3) * mm, "mid": v(14.58, -42.95) * mm, "end": v(15.5, -37.43) * mm});
            skArc(sketch, "E36.7.3", {"start": v(7.85, -29.3) * mm, "mid": v(11, -33.17) * mm, "end": v(14.57, -36.64) * mm});
            skArc(sketch, "E36.7.4", {"start": v(12.49, -46.6) * mm, "mid": v(13.83, -41.69) * mm, "end": v(14.57, -36.64) * mm});
            skArc(sketch, "E36.7.5", {"start": v(14.66, -35.39) * mm, "mid": v(14.62, -30.3) * mm, "end": v(13.97, -25.25) * mm});
            skArc(sketch, "E36.7.6", {"start": v(2.56, -19.46) * mm, "mid": v(4.52, -23.86) * mm, "end": v(6.96, -28) * mm});
            skArc(sketch, "E36.7.7", {"start": v(5, -37.98) * mm, "mid": v(6.28, -33.05) * mm, "end": v(6.96, -28) * mm});
            skArc(sketch, "E36.7.8", {"start": v(0.83, -6.33) * mm, "mid": v(1.14, -9.75) * mm, "end": v(1.73, -13.13) * mm});
            skArc(sketch, "E36.7.9", {"start": v(5.7, -39.02) * mm, "mid": v(8.86, -43.02) * mm, "end": v(12.49, -46.6) * mm});
            skArc(sketch, "E36.7.10", {"start": v(2.74, -16.93) * mm, "mid": v(4.6, -21.75) * mm, "end": v(7.05, -26.3) * mm});
            skArc(sketch, "E36.7.11", {"start": v(0.53, -28.85) * mm, "mid": v(2.49, -33.55) * mm, "end": v(5, -37.98) * mm});
            skLineSegment(sketch, "E36.7.12", {"start": v(0, 0) * mm, "end": v(25, -43.3) * mm, "construction": true});
            skArc(sketch, "E36.7.13", {"start": v(0, -8.59) * mm, "mid": v(0.65, -12.87) * mm, "end": v(1.73, -17.07) * mm});
            skArc(sketch, "E36.7.15", {"start": v(2.22, -8.3) * mm, "mid": v(3.96, -12.26) * mm, "end": v(6.1, -16.04) * mm});
            skArc(sketch, "E36.7.16", {"start": v(7.03, -15.65) * mm, "mid": v(10.08, -19.81) * mm, "end": v(13.61, -23.58) * mm});
            skArc(sketch, "E36.7.17", {"start": v(0, -50) * mm, "mid": v(2.97, -45.26) * mm, "end": v(5.29, -40.16) * mm});
            skArc(sketch, "E36.7.18", {"start": v(7.05, -26.3) * mm, "mid": v(6.89, -21.14) * mm, "end": v(6.1, -16.04) * mm});
            skArc(sketch, "E36.7.19", {"start": v(0, -30.33) * mm, "mid": v(2.04, -34.88) * mm, "end": v(4.6, -39.17) * mm});
            skArc(sketch, "E36.7.20", {"start": v(5.7, -39.02) * mm, "mid": v(7.06, -34.22) * mm, "end": v(7.85, -29.3) * mm});
            skArc(sketch, "E36.7.21", {"start": v(15.6, -36.21) * mm, "mid": v(19.7, -39.26) * mm, "end": v(24.12, -41.78) * mm});
            skArc(sketch, "E36.7.22", {"start": v(15.5, -37.43) * mm, "mid": v(20.06, -40.68) * mm, "end": v(25, -43.3) * mm});
            skLineSegment(sketch, "E36.7.23", {"start": v(0, -50) * mm, "end": v(0, 0) * mm, "construction": true});
            skArc(sketch, "E36.7.24", {"start": v(2.44, -5.9) * mm, "mid": v(3.63, -9.12) * mm, "end": v(5.07, -12.23) * mm});
            skArc(sketch, "E36.7.25", {"start": v(7.98, -27.73) * mm, "mid": v(8.02, -22.92) * mm, "end": v(7.51, -18.13) * mm});
            skArc(sketch, "E36.7.26", {"start": v(0, -27.22) * mm, "mid": v(1.18, -22.2) * mm, "end": v(1.73, -17.07) * mm});
            skArc(sketch, "E36.7.27", {"start": v(7.03, -15.65) * mm, "mid": v(5.87, -11.47) * mm, "end": v(4.3, -7.44) * mm});
            skArc(sketch, "E36.7.28", {"start": v(5.29, -40.16) * mm, "mid": v(8.85, -44.48) * mm, "end": v(12.94, -48.3) * mm});
            skArc(sketch, "E36.7.29", {"start": v(1.73, -13.13) * mm, "mid": v(1.42, -9.71) * mm, "end": v(0.83, -6.33) * mm});
            skArc(sketch, "E36.7.30", {"start": v(2.74, -16.93) * mm, "mid": v(2.7, -12.6) * mm, "end": v(2.22, -8.3) * mm});
            skArc(sketch, "E36.7.31", {"start": v(7.98, -27.73) * mm, "mid": v(11.08, -31.76) * mm, "end": v(14.66, -35.39) * mm});
            skPoint(sketch, "E36.7.32", {"position": v(-0.45, -1.7) * mm});
            skArc(sketch, "E36.7.33", {"start": v(15.6, -36.21) * mm, "mid": v(15.68, -31.23) * mm, "end": v(15.16, -26.27) * mm});
            skArc(sketch, "E36.7.34", {"start": v(0, -48.25) * mm, "mid": v(2.57, -43.85) * mm, "end": v(4.6, -39.17) * mm});
            skArc(sketch, "E36.7.35", {"start": v(5.07, -12.23) * mm, "mid": v(3.89, -9.01) * mm, "end": v(2.44, -5.9) * mm});
            skArc(sketch, "E36.7.36", {"start": v(0.8, -3) * mm, "mid": v(0.55, -2.6) * mm, "end": v(0.29, -2.19) * mm});
            skLineSegment(sketch, "E36.7.37", {"start": v(0.84, -2.04) * mm, "end": v(1.55, -2.69) * mm});
            skArc(sketch, "E36.7.38", {"start": v(0.29, -2.19) * mm, "mid": v(0.14, -2.65) * mm, "end": v(0, -3.1) * mm});
            skArc(sketch, "E36.7.39", {"start": v(0.84, -2.04) * mm, "mid": v(0.82, -2.52) * mm, "end": v(0.8, -3) * mm});
            skArc(sketch, "E36.8.0", {"start": v(15.57, -11.95) * mm, "mid": v(20.06, -13.67) * mm, "end": v(24.72, -14.88) * mm});
            skArc(sketch, "E36.8.1", {"start": v(14.88, -24.72) * mm, "mid": v(13.67, -20.06) * mm, "end": v(11.95, -15.57) * mm});
            skArc(sketch, "E36.8.2", {"start": v(35.36, -35.36) * mm, "mid": v(34.1, -29.9) * mm, "end": v(32.14, -24.66) * mm});
            skArc(sketch, "E36.8.3", {"start": v(21.45, -21.45) * mm, "mid": v(26.1, -23.22) * mm, "end": v(30.94, -24.45) * mm});
            skArc(sketch, "E36.8.4", {"start": v(34.12, -34.12) * mm, "mid": v(32.82, -29.19) * mm, "end": v(30.94, -24.45) * mm});
            skArc(sketch, "E36.8.5", {"start": v(30.39, -23.32) * mm, "mid": v(27.81, -18.93) * mm, "end": v(24.72, -14.88) * mm});
            skArc(sketch, "E36.8.6", {"start": v(11.95, -15.57) * mm, "mid": v(15.84, -18.4) * mm, "end": v(20.03, -20.78) * mm});
            skArc(sketch, "E36.8.7", {"start": v(23.32, -30.39) * mm, "mid": v(21.97, -25.48) * mm, "end": v(20.03, -20.78) * mm});
            skArc(sketch, "E36.8.8", {"start": v(3.89, -5.07) * mm, "mid": v(5.86, -7.87) * mm, "end": v(8.06, -10.5) * mm});
            skArc(sketch, "E36.8.9", {"start": v(24.45, -30.94) * mm, "mid": v(29.19, -32.82) * mm, "end": v(34.12, -34.12) * mm});
            skArc(sketch, "E36.8.10", {"start": v(10.84, -13.3) * mm, "mid": v(14.86, -16.53) * mm, "end": v(19.25, -19.25) * mm});
            skArc(sketch, "E36.8.11", {"start": v(14.88, -24.72) * mm, "mid": v(18.93, -27.81) * mm, "end": v(23.32, -30.39) * mm});
            skLineSegment(sketch, "E36.8.12", {"start": v(0, 0) * mm, "end": v(43.3, -25) * mm, "construction": true});
            skArc(sketch, "E36.8.13", {"start": v(4.3, -7.44) * mm, "mid": v(7, -10.82) * mm, "end": v(10.04, -13.91) * mm});
            skArc(sketch, "E36.8.15", {"start": v(6.07, -6.07) * mm, "mid": v(9.56, -8.64) * mm, "end": v(13.3, -10.84) * mm});
            skArc(sketch, "E36.8.16", {"start": v(13.91, -10.04) * mm, "mid": v(18.63, -12.12) * mm, "end": v(23.58, -13.61) * mm});
            skArc(sketch, "E36.8.17", {"start": v(25, -43.3) * mm, "mid": v(25.2, -37.7) * mm, "end": v(24.66, -32.14) * mm});
            skArc(sketch, "E36.8.18", {"start": v(19.25, -19.25) * mm, "mid": v(16.53, -14.86) * mm, "end": v(13.3, -10.84) * mm});
            skArc(sketch, "E36.8.19", {"start": v(15.16, -26.27) * mm, "mid": v(19.2, -29.19) * mm, "end": v(23.56, -31.62) * mm});
            skArc(sketch, "E36.8.20", {"start": v(24.45, -30.94) * mm, "mid": v(23.22, -26.1) * mm, "end": v(21.45, -21.45) * mm});
            skArc(sketch, "E36.8.21", {"start": v(31.62, -23.56) * mm, "mid": v(36.69, -24.15) * mm, "end": v(41.78, -24.12) * mm});
            skArc(sketch, "E36.8.22", {"start": v(32.14, -24.66) * mm, "mid": v(37.7, -25.2) * mm, "end": v(43.3, -25) * mm});
            skLineSegment(sketch, "E36.8.23", {"start": v(25, -43.3) * mm, "end": v(0, 0) * mm, "construction": true});
            skArc(sketch, "E36.8.24", {"start": v(5.07, -3.89) * mm, "mid": v(7.7, -6.09) * mm, "end": v(10.5, -8.06) * mm});
            skArc(sketch, "E36.8.25", {"start": v(20.78, -20.03) * mm, "mid": v(18.4, -15.84) * mm, "end": v(15.57, -11.95) * mm});
            skArc(sketch, "E36.8.26", {"start": v(13.61, -23.58) * mm, "mid": v(12.12, -18.63) * mm, "end": v(10.04, -13.91) * mm});
            skArc(sketch, "E36.8.27", {"start": v(13.91, -10.04) * mm, "mid": v(10.82, -7) * mm, "end": v(7.44, -4.3) * mm});
            skArc(sketch, "E36.8.28", {"start": v(24.66, -32.14) * mm, "mid": v(29.9, -34.1) * mm, "end": v(35.36, -35.36) * mm});
            skArc(sketch, "E36.8.29", {"start": v(8.06, -10.5) * mm, "mid": v(6.09, -7.7) * mm, "end": v(3.89, -5.07) * mm});
            skArc(sketch, "E36.8.30", {"start": v(10.84, -13.3) * mm, "mid": v(8.64, -9.56) * mm, "end": v(6.07, -6.07) * mm});
            skArc(sketch, "E36.8.31", {"start": v(20.78, -20.03) * mm, "mid": v(25.48, -21.97) * mm, "end": v(30.39, -23.32) * mm});
            skPoint(sketch, "E36.8.32", {"position": v(0.45, -1.7) * mm});
            skArc(sketch, "E36.8.33", {"start": v(31.62, -23.56) * mm, "mid": v(29.19, -19.2) * mm, "end": v(26.27, -15.16) * mm});
            skArc(sketch, "E36.8.34", {"start": v(24.12, -41.78) * mm, "mid": v(24.15, -36.69) * mm, "end": v(23.56, -31.62) * mm});
            skArc(sketch, "E36.8.35", {"start": v(10.5, -8.06) * mm, "mid": v(7.87, -5.86) * mm, "end": v(5.07, -3.89) * mm});
            skArc(sketch, "E36.8.36", {"start": v(2.2, -2.2) * mm, "mid": v(1.77, -1.97) * mm, "end": v(1.34, -1.75) * mm});
            skLineSegment(sketch, "E36.8.37", {"start": v(1.75, -1.34) * mm, "end": v(2.69, -1.55) * mm});
            skArc(sketch, "E36.8.38", {"start": v(1.34, -1.75) * mm, "mid": v(1.45, -2.22) * mm, "end": v(1.55, -2.69) * mm});
            skArc(sketch, "E36.8.39", {"start": v(1.75, -1.34) * mm, "mid": v(1.97, -1.77) * mm, "end": v(2.2, -2.2) * mm});
            skArc(sketch, "E36.9.0", {"start": v(19.46, -2.56) * mm, "mid": v(24.21, -1.8) * mm, "end": v(28.85, -0.53) * mm});
            skArc(sketch, "E36.9.1", {"start": v(25.25, -13.97) * mm, "mid": v(21.87, -10.54) * mm, "end": v(18.13, -7.51) * mm});
            skArc(sketch, "E36.9.2", {"start": v(48.3, -12.94) * mm, "mid": v(44.48, -8.85) * mm, "end": v(40.16, -5.29) * mm});
            skArc(sketch, "E36.9.3", {"start": v(29.3, -7.85) * mm, "mid": v(34.22, -7.06) * mm, "end": v(39.02, -5.7) * mm});
            skArc(sketch, "E36.9.4", {"start": v(46.6, -12.49) * mm, "mid": v(43.02, -8.86) * mm, "end": v(39.02, -5.7) * mm});
            skArc(sketch, "E36.9.5", {"start": v(37.98, -5) * mm, "mid": v(33.55, -2.49) * mm, "end": v(28.85, -0.53) * mm});
            skArc(sketch, "E36.9.6", {"start": v(18.13, -7.51) * mm, "mid": v(22.92, -8.02) * mm, "end": v(27.73, -7.98) * mm});
            skArc(sketch, "E36.9.7", {"start": v(35.39, -14.66) * mm, "mid": v(31.76, -11.08) * mm, "end": v(27.73, -7.98) * mm});
            skArc(sketch, "E36.9.8", {"start": v(5.9, -2.44) * mm, "mid": v(9.01, -3.89) * mm, "end": v(12.23, -5.07) * mm});
            skArc(sketch, "E36.9.9", {"start": v(36.64, -14.57) * mm, "mid": v(41.69, -13.83) * mm, "end": v(46.6, -12.49) * mm});
            skArc(sketch, "E36.9.10", {"start": v(16.04, -6.1) * mm, "mid": v(21.14, -6.89) * mm, "end": v(26.3, -7.05) * mm});
            skArc(sketch, "E36.9.11", {"start": v(25.25, -13.97) * mm, "mid": v(30.3, -14.62) * mm, "end": v(35.39, -14.66) * mm});
            skLineSegment(sketch, "E36.9.12", {"start": v(0, 0) * mm, "end": v(50, 0) * mm, "construction": true});
            skArc(sketch, "E36.9.13", {"start": v(7.44, -4.3) * mm, "mid": v(11.47, -5.87) * mm, "end": v(15.65, -7.03) * mm});
            skArc(sketch, "E36.9.15", {"start": v(8.3, -2.22) * mm, "mid": v(12.6, -2.7) * mm, "end": v(16.93, -2.74) * mm});
            skArc(sketch, "E36.9.16", {"start": v(17.07, -1.73) * mm, "mid": v(22.2, -1.18) * mm, "end": v(27.22, 0) * mm});
            skArc(sketch, "E36.9.17", {"start": v(43.3, -25) * mm, "mid": v(40.68, -20.06) * mm, "end": v(37.43, -15.5) * mm});
            skArc(sketch, "E36.9.18", {"start": v(26.3, -7.05) * mm, "mid": v(21.75, -4.6) * mm, "end": v(16.93, -2.74) * mm});
            skArc(sketch, "E36.9.19", {"start": v(26.27, -15.16) * mm, "mid": v(31.23, -15.68) * mm, "end": v(36.21, -15.6) * mm});
            skArc(sketch, "E36.9.20", {"start": v(36.64, -14.57) * mm, "mid": v(33.17, -11) * mm, "end": v(29.3, -7.85) * mm});
            skArc(sketch, "E36.9.21", {"start": v(39.17, -4.6) * mm, "mid": v(43.85, -2.57) * mm, "end": v(48.25, 0) * mm});
            skArc(sketch, "E36.9.22", {"start": v(40.16, -5.29) * mm, "mid": v(45.26, -2.97) * mm, "end": v(50, 0) * mm});
            skLineSegment(sketch, "E36.9.23", {"start": v(43.3, -25) * mm, "end": v(0, 0) * mm, "construction": true});
            skArc(sketch, "E36.9.24", {"start": v(6.33, -0.83) * mm, "mid": v(9.71, -1.42) * mm, "end": v(13.13, -1.73) * mm});
            skArc(sketch, "E36.9.25", {"start": v(28, -6.96) * mm, "mid": v(23.86, -4.52) * mm, "end": v(19.46, -2.56) * mm});
            skArc(sketch, "E36.9.26", {"start": v(23.58, -13.61) * mm, "mid": v(19.81, -10.08) * mm, "end": v(15.65, -7.03) * mm});
            skArc(sketch, "E36.9.27", {"start": v(17.07, -1.73) * mm, "mid": v(12.87, -0.65) * mm, "end": v(8.59, 0) * mm});
            skArc(sketch, "E36.9.28", {"start": v(37.43, -15.5) * mm, "mid": v(42.95, -14.58) * mm, "end": v(48.3, -12.94) * mm});
            skArc(sketch, "E36.9.29", {"start": v(12.23, -5.07) * mm, "mid": v(9.12, -3.63) * mm, "end": v(5.9, -2.44) * mm});
            skArc(sketch, "E36.9.30", {"start": v(16.04, -6.1) * mm, "mid": v(12.26, -3.96) * mm, "end": v(8.3, -2.22) * mm});
            skArc(sketch, "E36.9.31", {"start": v(28, -6.96) * mm, "mid": v(33.05, -6.28) * mm, "end": v(37.98, -5) * mm});
            skPoint(sketch, "E36.9.32", {"position": v(1.24, -1.24) * mm});
            skArc(sketch, "E36.9.33", {"start": v(39.17, -4.6) * mm, "mid": v(34.88, -2.04) * mm, "end": v(30.33, 0) * mm});
            skArc(sketch, "E36.9.34", {"start": v(41.78, -24.12) * mm, "mid": v(39.26, -19.7) * mm, "end": v(36.21, -15.6) * mm});
            skArc(sketch, "E36.9.35", {"start": v(13.13, -1.73) * mm, "mid": v(9.75, -1.14) * mm, "end": v(6.33, -0.83) * mm});
            skArc(sketch, "E36.9.36", {"start": v(3, -0.8) * mm, "mid": v(2.52, -0.82) * mm, "end": v(2.04, -0.84) * mm});
            skLineSegment(sketch, "E36.9.37", {"start": v(2.19, -0.29) * mm, "end": v(3.1, 0) * mm});
            skArc(sketch, "E36.9.38", {"start": v(2.04, -0.84) * mm, "mid": v(2.36, -1.2) * mm, "end": v(2.69, -1.55) * mm});
            skArc(sketch, "E36.9.39", {"start": v(2.19, -0.29) * mm, "mid": v(2.6, -0.55) * mm, "end": v(3, -0.8) * mm});
            skArc(sketch, "E36.10.0", {"start": v(18.13, 7.51) * mm, "mid": v(21.87, 10.54) * mm, "end": v(25.25, 13.97) * mm});
            skArc(sketch, "E36.10.1", {"start": v(28.85, 0.53) * mm, "mid": v(24.21, 1.8) * mm, "end": v(19.46, 2.56) * mm});
            skArc(sketch, "E36.10.2", {"start": v(48.3, 12.94) * mm, "mid": v(42.95, 14.58) * mm, "end": v(37.43, 15.5) * mm});
            skArc(sketch, "E36.10.3", {"start": v(29.3, 7.85) * mm, "mid": v(33.17, 11) * mm, "end": v(36.64, 14.57) * mm});
            skArc(sketch, "E36.10.4", {"start": v(46.6, 12.49) * mm, "mid": v(41.69, 13.83) * mm, "end": v(36.64, 14.57) * mm});
            skArc(sketch, "E36.10.5", {"start": v(35.39, 14.66) * mm, "mid": v(30.3, 14.62) * mm, "end": v(25.25, 13.97) * mm});
            skArc(sketch, "E36.10.6", {"start": v(19.46, 2.56) * mm, "mid": v(23.86, 4.52) * mm, "end": v(28, 6.96) * mm});
            skArc(sketch, "E36.10.7", {"start": v(37.98, 5) * mm, "mid": v(33.05, 6.28) * mm, "end": v(28, 6.96) * mm});
            skArc(sketch, "E36.10.8", {"start": v(6.33, 0.83) * mm, "mid": v(9.75, 1.14) * mm, "end": v(13.13, 1.73) * mm});
            skArc(sketch, "E36.10.9", {"start": v(39.02, 5.7) * mm, "mid": v(43.02, 8.86) * mm, "end": v(46.6, 12.49) * mm});
            skArc(sketch, "E36.10.10", {"start": v(16.93, 2.74) * mm, "mid": v(21.75, 4.6) * mm, "end": v(26.3, 7.05) * mm});
            skArc(sketch, "E36.10.11", {"start": v(28.85, 0.53) * mm, "mid": v(33.55, 2.49) * mm, "end": v(37.98, 5) * mm});
            skLineSegment(sketch, "E36.10.12", {"start": v(0, 0) * mm, "end": v(43.3, 25) * mm, "construction": true});
            skArc(sketch, "E36.10.13", {"start": v(8.59, 0) * mm, "mid": v(12.87, 0.65) * mm, "end": v(17.07, 1.73) * mm});
            skArc(sketch, "E36.10.15", {"start": v(8.3, 2.22) * mm, "mid": v(12.26, 3.96) * mm, "end": v(16.04, 6.1) * mm});
            skArc(sketch, "E36.10.16", {"start": v(15.65, 7.03) * mm, "mid": v(19.81, 10.08) * mm, "end": v(23.58, 13.61) * mm});
            skArc(sketch, "E36.10.17", {"start": v(50, 0) * mm, "mid": v(45.26, 2.97) * mm, "end": v(40.16, 5.29) * mm});
            skArc(sketch, "E36.10.18", {"start": v(26.3, 7.05) * mm, "mid": v(21.14, 6.89) * mm, "end": v(16.04, 6.1) * mm});
            skArc(sketch, "E36.10.19", {"start": v(30.33, 0) * mm, "mid": v(34.88, 2.04) * mm, "end": v(39.17, 4.6) * mm});
            skArc(sketch, "E36.10.20", {"start": v(39.02, 5.7) * mm, "mid": v(34.22, 7.06) * mm, "end": v(29.3, 7.85) * mm});
            skArc(sketch, "E36.10.21", {"start": v(36.21, 15.6) * mm, "mid": v(39.26, 19.7) * mm, "end": v(41.78, 24.12) * mm});
            skArc(sketch, "E36.10.22", {"start": v(37.43, 15.5) * mm, "mid": v(40.68, 20.06) * mm, "end": v(43.3, 25) * mm});
            skLineSegment(sketch, "E36.10.23", {"start": v(50, 0) * mm, "end": v(0, 0) * mm, "construction": true});
            skArc(sketch, "E36.10.24", {"start": v(5.9, 2.44) * mm, "mid": v(9.12, 3.63) * mm, "end": v(12.23, 5.07) * mm});
            skArc(sketch, "E36.10.25", {"start": v(27.73, 7.98) * mm, "mid": v(22.92, 8.02) * mm, "end": v(18.13, 7.51) * mm});
            skArc(sketch, "E36.10.26", {"start": v(27.22, 0) * mm, "mid": v(22.2, 1.18) * mm, "end": v(17.07, 1.73) * mm});
            skArc(sketch, "E36.10.27", {"start": v(15.65, 7.03) * mm, "mid": v(11.47, 5.87) * mm, "end": v(7.44, 4.3) * mm});
            skArc(sketch, "E36.10.28", {"start": v(40.16, 5.29) * mm, "mid": v(44.48, 8.85) * mm, "end": v(48.3, 12.94) * mm});
            skArc(sketch, "E36.10.29", {"start": v(13.13, 1.73) * mm, "mid": v(9.71, 1.42) * mm, "end": v(6.33, 0.83) * mm});
            skArc(sketch, "E36.10.30", {"start": v(16.93, 2.74) * mm, "mid": v(12.6, 2.7) * mm, "end": v(8.3, 2.22) * mm});
            skArc(sketch, "E36.10.31", {"start": v(27.73, 7.98) * mm, "mid": v(31.76, 11.08) * mm, "end": v(35.39, 14.66) * mm});
            skPoint(sketch, "E36.10.32", {"position": v(1.7, -0.45) * mm});
            skArc(sketch, "E36.10.33", {"start": v(36.21, 15.6) * mm, "mid": v(31.23, 15.68) * mm, "end": v(26.27, 15.16) * mm});
            skArc(sketch, "E36.10.34", {"start": v(48.25, 0) * mm, "mid": v(43.85, 2.57) * mm, "end": v(39.17, 4.6) * mm});
            skArc(sketch, "E36.10.35", {"start": v(12.23, 5.07) * mm, "mid": v(9.01, 3.89) * mm, "end": v(5.9, 2.44) * mm});
            skArc(sketch, "E36.10.36", {"start": v(3, 0.8) * mm, "mid": v(2.6, 0.55) * mm, "end": v(2.19, 0.29) * mm});
            skLineSegment(sketch, "E36.10.37", {"start": v(2.04, 0.84) * mm, "end": v(2.69, 1.55) * mm});
            skArc(sketch, "E36.10.38", {"start": v(2.19, 0.29) * mm, "mid": v(2.65, 0.14) * mm, "end": v(3.1, 0) * mm});
            skArc(sketch, "E36.10.39", {"start": v(2.04, 0.84) * mm, "mid": v(2.52, 0.82) * mm, "end": v(3, 0.8) * mm});
            skArc(sketch, "E36.11.0", {"start": v(11.95, 15.57) * mm, "mid": v(13.67, 20.06) * mm, "end": v(14.88, 24.72) * mm});
            skArc(sketch, "E36.11.1", {"start": v(24.72, 14.88) * mm, "mid": v(20.06, 13.67) * mm, "end": v(15.57, 11.95) * mm});
            skArc(sketch, "E36.11.2", {"start": v(35.36, 35.36) * mm, "mid": v(29.9, 34.1) * mm, "end": v(24.66, 32.14) * mm});
            skArc(sketch, "E36.11.3", {"start": v(21.45, 21.45) * mm, "mid": v(23.22, 26.1) * mm, "end": v(24.45, 30.94) * mm});
            skArc(sketch, "E36.11.4", {"start": v(34.12, 34.12) * mm, "mid": v(29.19, 32.82) * mm, "end": v(24.45, 30.94) * mm});
            skArc(sketch, "E36.11.5", {"start": v(23.32, 30.39) * mm, "mid": v(18.93, 27.81) * mm, "end": v(14.88, 24.72) * mm});
            skArc(sketch, "E36.11.6", {"start": v(15.57, 11.95) * mm, "mid": v(18.4, 15.84) * mm, "end": v(20.78, 20.03) * mm});
            skArc(sketch, "E36.11.7", {"start": v(30.39, 23.32) * mm, "mid": v(25.48, 21.97) * mm, "end": v(20.78, 20.03) * mm});
            skArc(sketch, "E36.11.8", {"start": v(5.07, 3.89) * mm, "mid": v(7.87, 5.86) * mm, "end": v(10.5, 8.06) * mm});
            skArc(sketch, "E36.11.9", {"start": v(30.94, 24.45) * mm, "mid": v(32.82, 29.19) * mm, "end": v(34.12, 34.12) * mm});
            skArc(sketch, "E36.11.10", {"start": v(13.3, 10.84) * mm, "mid": v(16.53, 14.86) * mm, "end": v(19.25, 19.25) * mm});
            skArc(sketch, "E36.11.11", {"start": v(24.72, 14.88) * mm, "mid": v(27.81, 18.93) * mm, "end": v(30.39, 23.32) * mm});
            skLineSegment(sketch, "E36.11.12", {"start": v(0, 0) * mm, "end": v(25, 43.3) * mm, "construction": true});
            skArc(sketch, "E36.11.13", {"start": v(7.44, 4.3) * mm, "mid": v(10.82, 7) * mm, "end": v(13.91, 10.04) * mm});
            skArc(sketch, "E36.11.15", {"start": v(6.07, 6.07) * mm, "mid": v(8.64, 9.56) * mm, "end": v(10.84, 13.3) * mm});
            skArc(sketch, "E36.11.16", {"start": v(10.04, 13.91) * mm, "mid": v(12.12, 18.63) * mm, "end": v(13.61, 23.58) * mm});
            skArc(sketch, "E36.11.17", {"start": v(43.3, 25) * mm, "mid": v(37.7, 25.2) * mm, "end": v(32.14, 24.66) * mm});
            skArc(sketch, "E36.11.18", {"start": v(19.25, 19.25) * mm, "mid": v(14.86, 16.53) * mm, "end": v(10.84, 13.3) * mm});
            skArc(sketch, "E36.11.19", {"start": v(26.27, 15.16) * mm, "mid": v(29.19, 19.2) * mm, "end": v(31.62, 23.56) * mm});
            skArc(sketch, "E36.11.20", {"start": v(30.94, 24.45) * mm, "mid": v(26.1, 23.22) * mm, "end": v(21.45, 21.45) * mm});
            skArc(sketch, "E36.11.21", {"start": v(23.56, 31.62) * mm, "mid": v(24.15, 36.69) * mm, "end": v(24.12, 41.78) * mm});
            skArc(sketch, "E36.11.22", {"start": v(24.66, 32.14) * mm, "mid": v(25.2, 37.7) * mm, "end": v(25, 43.3) * mm});
            skLineSegment(sketch, "E36.11.23", {"start": v(43.3, 25) * mm, "end": v(0, 0) * mm, "construction": true});
            skArc(sketch, "E36.11.24", {"start": v(3.89, 5.07) * mm, "mid": v(6.09, 7.7) * mm, "end": v(8.06, 10.5) * mm});
            skArc(sketch, "E36.11.25", {"start": v(20.03, 20.78) * mm, "mid": v(15.84, 18.4) * mm, "end": v(11.95, 15.57) * mm});
            skArc(sketch, "E36.11.26", {"start": v(23.58, 13.61) * mm, "mid": v(18.63, 12.12) * mm, "end": v(13.91, 10.04) * mm});
            skArc(sketch, "E36.11.27", {"start": v(10.04, 13.91) * mm, "mid": v(7, 10.82) * mm, "end": v(4.3, 7.44) * mm});
            skArc(sketch, "E36.11.28", {"start": v(32.14, 24.66) * mm, "mid": v(34.1, 29.9) * mm, "end": v(35.36, 35.36) * mm});
            skArc(sketch, "E36.11.29", {"start": v(10.5, 8.06) * mm, "mid": v(7.7, 6.09) * mm, "end": v(5.07, 3.89) * mm});
            skArc(sketch, "E36.11.30", {"start": v(13.3, 10.84) * mm, "mid": v(9.56, 8.64) * mm, "end": v(6.07, 6.07) * mm});
            skArc(sketch, "E36.11.31", {"start": v(20.03, 20.78) * mm, "mid": v(21.97, 25.48) * mm, "end": v(23.32, 30.39) * mm});
            skPoint(sketch, "E36.11.32", {"position": v(1.7, 0.45) * mm});
            skArc(sketch, "E36.11.33", {"start": v(23.56, 31.62) * mm, "mid": v(19.2, 29.19) * mm, "end": v(15.16, 26.27) * mm});
            skArc(sketch, "E36.11.34", {"start": v(41.78, 24.12) * mm, "mid": v(36.69, 24.15) * mm, "end": v(31.62, 23.56) * mm});
            skArc(sketch, "E36.11.35", {"start": v(8.06, 10.5) * mm, "mid": v(5.86, 7.87) * mm, "end": v(3.89, 5.07) * mm});
            skArc(sketch, "E36.11.36", {"start": v(2.2, 2.2) * mm, "mid": v(1.97, 1.77) * mm, "end": v(1.75, 1.34) * mm});
            skLineSegment(sketch, "E36.11.37", {"start": v(1.34, 1.75) * mm, "end": v(1.55, 2.69) * mm});
            skArc(sketch, "E36.11.38", {"start": v(1.75, 1.34) * mm, "mid": v(2.22, 1.45) * mm, "end": v(2.69, 1.55) * mm});
            skArc(sketch, "E36.11.39", {"start": v(1.34, 1.75) * mm, "mid": v(1.77, 1.97) * mm, "end": v(2.2, 2.2) * mm});
            skSolve(sketch);
        }
        {
            var Q0;
            Q0 = qSketchRegion(id + "F0", true);
            extrude(context, id + "F1", {"entities" : qUnion([Q0]), "depth" : 1 * mm, "offsetDistance" : 25 * mm});
        }
    });
